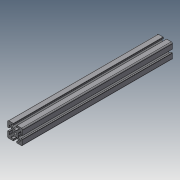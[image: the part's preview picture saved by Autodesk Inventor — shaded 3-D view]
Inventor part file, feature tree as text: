
AUTODESK INVENTOR PART (.ipt)
format: ipt  version: 2018.3 (Build 223284000, 284)  size: 238,592 bytes
history: native  units: in
note: dims shown in document units (in); Inventor stores cm internally (conversion verified against a paired STEP export)
features: extrude x1, sketch x1, projected_geometry x1
ambient origin geometry x8: Origin, YZ Plane, XZ Plane, XY Plane, X Axis, Y Axis, Z Axis, Center Point
bodies: Body1 (feature_tree)
feature tree (3):
  extrude  "Extrusion1"  [1 undecoded]
  sketch  "Sketch1"  dims[d0=15.525in d1=0.0in]
  projected_geometry  "Projected Loop1"
note: 1 required parameter value undecoded (feature->parameter linkage not recoverable at this tier; creation-order binding heuristic only, values carry confidence <= 0.55)
